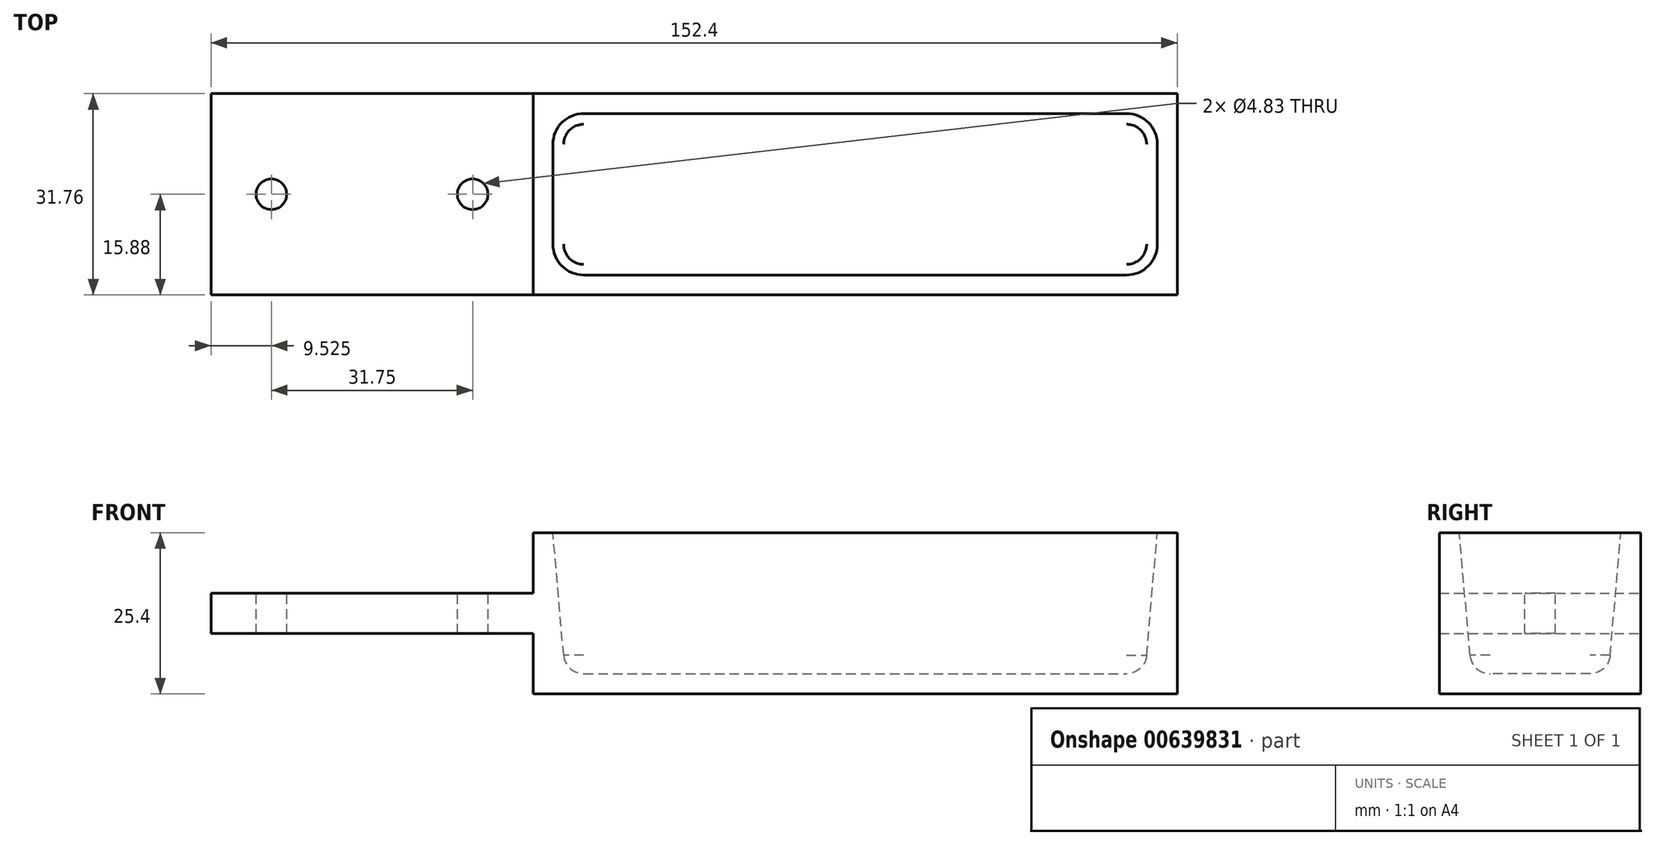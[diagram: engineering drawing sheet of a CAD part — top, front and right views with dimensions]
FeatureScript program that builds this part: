
annotation { "Feature Type Name" : "Feature", "Feature Type Description" : "" }
export const myFeature = defineFeature(function(context is Context, id is Id, definition is map)
    precondition{}
    {
        {
            var Q0;
            Q0=qCreatedBy(makeId("Top.planeOp"),FACE);
            var sketch = newSketch(context, id + "F0", { "sketchPlane" : qUnion([Q0])});
            skLineSegment(sketch, "E0.bottom", {"start": v(-50.8, 15.88) * mm, "end": v(50.8, 15.88) * mm});
            skLineSegment(sketch, "E0.top", {"start": v(-50.8, -15.87) * mm, "end": v(50.8, -15.87) * mm});
            skLineSegment(sketch, "E0.left", {"start": v(-50.8, 15.87) * mm, "end": v(-50.8, -15.87) * mm, "construction": true});
            skLineSegment(sketch, "E0.right", {"start": v(50.8, 15.87) * mm, "end": v(50.8, -15.87) * mm});
            skPoint(sketch, "E1", {"position": v(0, 15.88) * mm});
            skPoint(sketch, "E2", {"position": v(50.8, 0) * mm});
            skLineSegment(sketch, "E3", {"start": v(-50.8, 15.88) * mm, "end": v(-101.6, 15.88) * mm});
            skLineSegment(sketch, "E4", {"start": v(-101.6, 15.87) * mm, "end": v(-101.6, -15.87) * mm});
            skLineSegment(sketch, "E5", {"start": v(-101.6, -15.87) * mm, "end": v(-50.8, -15.87) * mm});
            skSolve(sketch);
        }
        {
            var Q0;
            Q0=makeQuery(id+"F0.imprint","IMPRINT",FACE,{"disambiguationData":[TD([[makeQuery(id+"F0.imprint","IMPRINT",EDGE,{"derivedFrom":sQuery(id+"F0.wireOp",EDGE,"E0.bottom")}),-1.0]])]});
            var Q1;
            Q1=sQuery(id+"F0.wireOp",EDGE,"E0.left");
            extrude(context, id + "F1", {"entities" : qUnion([Q0]), "surfaceEntities" : qUnion([Q1]), "depth" : 25.4 * mm, "offsetDistance" : 25.4 * mm});
        }
        {
            var Q0;
            Q0=qCreatedBy(makeId("Front.planeOp"),FACE);
            var sketch = newSketch(context, id + "F2", { "sketchPlane" : qUnion([Q0])});
            skLineSegment(sketch, "E6.bottom", {"start": v(-101.6, 25.4) * mm, "end": v(-50.8, 25.4) * mm});
            skLineSegment(sketch, "E6.top", {"start": v(-101.6, 15.88) * mm, "end": v(-50.8, 15.88) * mm});
            skLineSegment(sketch, "E6.left", {"start": v(-101.6, 25.4) * mm, "end": v(-101.6, 15.88) * mm});
            skLineSegment(sketch, "E6.right", {"start": v(-50.8, 25.4) * mm, "end": v(-50.8, 15.88) * mm});
            skLineSegment(sketch, "E7.bottom", {"start": v(-101.6, 0) * mm, "end": v(-50.8, 0) * mm});
            skLineSegment(sketch, "E7.top", {"start": v(-101.6, 9.53) * mm, "end": v(-50.8, 9.53) * mm});
            skLineSegment(sketch, "E7.left", {"start": v(-101.6, 0) * mm, "end": v(-101.6, 9.53) * mm});
            skLineSegment(sketch, "E7.right", {"start": v(-50.8, 0) * mm, "end": v(-50.8, 9.53) * mm});
            skSolve(sketch);
        }
        {
            var Q0;
            Q0 = qSketchRegion(id + "F2", true);
            extrude(context, id + "F3", {"entities" : qUnion([Q0]), "operationType" : NewBodyOperationType.REMOVE, "endBound" : BoundingType.THROUGH_ALL, "depth" : 25.4 * mm, "offsetDistance" : 25.4 * mm, "hasSecondDirection" : true, "secondDirectionOppositeDirection" : true, "secondDirectionDepth" : 50.8 * mm});
        }
        {
            var Q0;
            Q0=qCreatedBy(makeId("Front.planeOp"),FACE);
            var sketch = newSketch(context, id + "F4", { "sketchPlane" : qUnion([Q0])});
            skLineSegment(sketch, "E8", {"start": v(47.38, 22.18) * mm, "end": v(45.97, 6.07) * mm});
            skLineSegment(sketch, "E9", {"start": v(42.81, 25.4) * mm, "end": v(42.81, 3.18) * mm, "construction": true});
            skArc(sketch, "E10.filletArc", {"start": v(42.81, 3.18) * mm, "mid": v(44.96, 4) * mm, "end": v(45.97, 6.07) * mm});
            skPoint(sketch, "E11", {"position": v(47.38, 22.18) * mm});
            skLineSegment(sketch, "E12", {"start": v(47.38, 22.18) * mm, "end": v(47.89, 27.94) * mm});
            skLineSegment(sketch, "E13", {"start": v(45.97, 6.07) * mm, "end": v(45.72, 3.17) * mm, "construction": true});
            skLineSegment(sketch, "E14", {"start": v(45.72, 3.18) * mm, "end": v(42.81, 3.18) * mm, "construction": true});
            skPoint(sketch, "E15", {"position": v(47.66, 25.4) * mm});
            skLineSegment(sketch, "E16.0.1", {"start": v(-50.8, 25.4) * mm, "end": v(50.8, 25.4) * mm});
            skLineSegment(sketch, "E16.0.3", {"start": v(50.8, 25.4) * mm, "end": v(-50.8, 25.4) * mm});
            skSolve(sketch);
        }
        {
            var Q0;
            Q0=qCreatedBy(makeId("Right.planeOp"),FACE);
            var sketch = newSketch(context, id + "F5", { "sketchPlane" : qUnion([Q0])});
            skLineSegment(sketch, "E17.0", {"start": v(15.88, 25.4) * mm, "end": v(-15.87, 25.4) * mm});
            skLineSegment(sketch, "E18.0", {"start": v(15.88, 0) * mm, "end": v(-15.87, 0) * mm});
            skLineSegment(sketch, "E19.0", {"start": v(15.88, 25.4) * mm, "end": v(15.88, 0) * mm});
            skLineSegment(sketch, "E20", {"start": v(12.74, 25.4) * mm, "end": v(11.05, 6.07) * mm});
            skLineSegment(sketch, "E21", {"start": v(7.89, 3.18) * mm, "end": v(0, 3.18) * mm});
            skPoint(sketch, "E22.visualSharp", {"position": v(10.8, 3.18) * mm});
            skArc(sketch, "E22.filletArc", {"start": v(7.89, 3.18) * mm, "mid": v(10.03, 4) * mm, "end": v(11.05, 6.07) * mm});
            skLineSegment(sketch, "E23", {"start": v(11.05, 6.07) * mm, "end": v(10.8, 3.18) * mm, "construction": true});
            skLineSegment(sketch, "E24", {"start": v(7.89, 3.18) * mm, "end": v(10.8, 3.18) * mm, "construction": true});
            skLineSegment(sketch, "E25", {"start": v(11.43, 25.4) * mm, "end": v(11.43, 20.32) * mm});
            skLineSegment(sketch, "E26", {"start": v(11.43, 20.32) * mm, "end": v(10.92, 20.32) * mm});
            skLineSegment(sketch, "E27", {"start": v(10.92, 20.32) * mm, "end": v(10.92, 15.24) * mm});
            skLineSegment(sketch, "E28", {"start": v(10.92, 15.24) * mm, "end": v(10.41, 15.24) * mm});
            skLineSegment(sketch, "E29", {"start": v(10.41, 15.24) * mm, "end": v(10.41, 10.16) * mm});
            skLineSegment(sketch, "E30", {"start": v(10.41, 10.16) * mm, "end": v(9.9, 10.16) * mm});
            skLineSegment(sketch, "E31", {"start": v(9.9, 10.16) * mm, "end": v(9.9, 5.08) * mm});
            skLineSegment(sketch, "E32", {"start": v(9.9, 5.08) * mm, "end": v(7.37, 5.08) * mm});
            skLineSegment(sketch, "E33", {"start": v(7.37, 5.08) * mm, "end": v(7.37, 3.18) * mm});
            skLineSegment(sketch, "E34", {"start": v(11.46, 25.4) * mm, "end": v(9.52, 3.18) * mm});
            skLineSegment(sketch, "E35", {"start": v(10.92, 17.11) * mm, "end": v(1.44, 17.11) * mm});
            skPoint(sketch, "E36", {"position": v(6.18, 17.11) * mm});
            skSolve(sketch);
        }
        {
            var Q0;
            Q0=qCreatedBy(makeId("Front.planeOp"),FACE);
            var sketch = newSketch(context, id + "F6", { "sketchPlane" : qUnion([Q0])});
            skLineSegment(sketch, "E37.0", {"start": v(47.38, 22.18) * mm, "end": v(45.97, 6.07) * mm});
            skLineSegment(sketch, "E38.0", {"start": v(47.38, 22.18) * mm, "end": v(47.89, 27.94) * mm});
            skLineSegment(sketch, "E39.0.1", {"start": v(-50.8, 25.4) * mm, "end": v(50.8, 25.4) * mm});
            skLineSegment(sketch, "E39.0.3", {"start": v(50.8, 25.4) * mm, "end": v(-50.8, 25.4) * mm});
            skLineSegment(sketch, "E40", {"start": v(46.23, 25.4) * mm, "end": v(46.23, 20.32) * mm});
            skLineSegment(sketch, "E41", {"start": v(46.23, 20.32) * mm, "end": v(45.72, 20.32) * mm});
            skLineSegment(sketch, "E42", {"start": v(45.72, 20.32) * mm, "end": v(45.72, 15.24) * mm});
            skLineSegment(sketch, "E43", {"start": v(45.72, 15.24) * mm, "end": v(45.21, 15.24) * mm});
            skLineSegment(sketch, "E44", {"start": v(45.21, 15.24) * mm, "end": v(45.21, 10.16) * mm});
            skLineSegment(sketch, "E45", {"start": v(45.21, 10.16) * mm, "end": v(44.7, 10.16) * mm});
            skLineSegment(sketch, "E46", {"start": v(44.7, 10.16) * mm, "end": v(44.7, 5.08) * mm});
            skLineSegment(sketch, "E47", {"start": v(44.7, 5.08) * mm, "end": v(42.16, 5.08) * mm});
            skLineSegment(sketch, "E48", {"start": v(42.16, 5.08) * mm, "end": v(42.16, 3.18) * mm});
            skLineSegment(sketch, "E49", {"start": v(46.39, 25.4) * mm, "end": v(44.17, 0) * mm});
            skLineSegment(sketch, "E50.0", {"start": v(42.81, 25.4) * mm, "end": v(42.81, 3.18) * mm});
            skLineSegment(sketch, "E51", {"start": v(42.16, 3.18) * mm, "end": v(0, 3.17) * mm});
            skSolve(sketch);
        }
        {
            var Q0;
            Q0=makeQuery(id+"F1.opExtrude","CAP_FACE",FACE,{"disambiguationData":[OSD([sQuery(id+"F0.wireOp",EDGE,"E0.bottom"),sQuery(id+"F0.wireOp",EDGE,"E0.top"),sQuery(id+"F0.wireOp",EDGE,"E0.right"),sQuery(id+"F0.wireOp",EDGE,"E3"),sQuery(id+"F0.wireOp",EDGE,"E4"),sQuery(id+"F0.wireOp",EDGE,"E5")])],"isStart":true});
            cPlane(context, id + "F7", {"entities" : qUnion([Q0]), "cplaneType" : CPlaneType.OFFSET, "offset" : 3.17 * mm, "oppositeDirection" : true, "width" : 152.4 * mm, "height" : 152.4 * mm});
        }
        {
            var Q0;
            Q0=qCreatedBy(id+"F7.planeOp",FACE);
            var sketch = newSketch(context, id + "F8", { "sketchPlane" : qUnion([Q0])});
            skPoint(sketch, "E52.0", {"position": v(45.72, 0) * mm});
            skLineSegment(sketch, "E53.bottom", {"start": v(-42.81, -10.8) * mm, "end": v(42.81, -10.8) * mm});
            skLineSegment(sketch, "E53.top", {"start": v(-42.81, 10.8) * mm, "end": v(42.81, 10.8) * mm});
            skLineSegment(sketch, "E53.left", {"start": v(-45.72, -7.89) * mm, "end": v(-45.72, 7.89) * mm});
            skLineSegment(sketch, "E53.right", {"start": v(45.72, -7.89) * mm, "end": v(45.72, 7.89) * mm});
            skPoint(sketch, "E54", {"position": v(0, -10.8) * mm});
            skPoint(sketch, "E55.visualSharp", {"position": v(45.72, -10.8) * mm});
            skArc(sketch, "E55.filletArc", {"start": v(42.81, -10.8) * mm, "mid": v(44.87, -9.94) * mm, "end": v(45.72, -7.89) * mm});
            skPoint(sketch, "E56.visualSharp", {"position": v(45.72, 10.8) * mm});
            skArc(sketch, "E56.filletArc", {"start": v(45.72, 7.89) * mm, "mid": v(44.87, 9.94) * mm, "end": v(42.81, 10.8) * mm});
            skPoint(sketch, "E57.visualSharp", {"position": v(-45.72, -10.8) * mm});
            skArc(sketch, "E57.filletArc", {"start": v(-45.72, -7.89) * mm, "mid": v(-44.87, -9.94) * mm, "end": v(-42.81, -10.8) * mm});
            skPoint(sketch, "E58.visualSharp", {"position": v(-45.72, 10.8) * mm});
            skArc(sketch, "E58.filletArc", {"start": v(-42.81, 10.8) * mm, "mid": v(-44.87, 9.94) * mm, "end": v(-45.72, 7.89) * mm});
            skSolve(sketch);
        }
        {
            var Q0;
            Q0=makeQuery(id+"F8.imprint","IMPRINT",FACE,{"disambiguationData":[TD([[makeQuery(id+"F8.imprint","IMPRINT",EDGE,{"derivedFrom":sQuery(id+"F8.wireOp",EDGE,"E53.bottom")}),1.0]])]});
            extrude(context, id + "F9", {"entities" : qUnion([Q0]), "operationType" : NewBodyOperationType.REMOVE, "oppositeDirection" : true, "depth" : 25.4 * mm, "offsetDistance" : 25.4 * mm, "hasDraft" : true, "draftAngle" : 5 * degree});
        }
        {
            var Q0;
            Q0=makeQuery(id+"F9.boolean.opBoolean","COPY",EDGE,{"derivedFrom":makeQuery(id+"F9.opExtrude","CAP_EDGE",EDGE,{"disambiguationData":[OSD([sQuery(id+"F8.wireOp",EDGE,"E55.filletArc")])],"isStart":true})});
            fillet(context, id + "F10", {"entities" : qUnion([Q0]), "radius" : 3.17 * mm, "tangentPropagation" : true, "allowEdgeOverflow" : false});
        }
        {
            var Q0;
            Q0=makeQuery(id+"F1.opExtrude","CAP_FACE",FACE,{"disambiguationData":[OSD([sQuery(id+"F0.wireOp",EDGE,"E0.bottom"),sQuery(id+"F0.wireOp",EDGE,"E0.top"),sQuery(id+"F0.wireOp",EDGE,"E0.right"),sQuery(id+"F0.wireOp",EDGE,"E3"),sQuery(id+"F0.wireOp",EDGE,"E4"),sQuery(id+"F0.wireOp",EDGE,"E5")])],"isStart":false});
            var sketch = newSketch(context, id + "F11", { "sketchPlane" : qUnion([Q0])});
            skLineSegment(sketch, "E59.0", {"start": v(-50.8, 15.88) * mm, "end": v(50.8, 15.88) * mm});
            skLineSegment(sketch, "E60.0", {"start": v(42.81, 12.74) * mm, "end": v(-42.81, 12.74) * mm});
            skLineSegment(sketch, "E61.0", {"start": v(47.66, -7.89) * mm, "end": v(47.66, 7.89) * mm});
            skLineSegment(sketch, "E62.0", {"start": v(50.8, 15.88) * mm, "end": v(50.8, -15.87) * mm});
            skSolve(sketch);
        }
        {
            var Q0;
            Q0=makeQuery(id+"F3.boolean.opBoolean","COPY",FACE,{"derivedFrom":makeQuery(id+"F3.opExtrude","SWEPT_FACE",FACE,{"disambiguationData":[OSD([sQuery(id+"F2.wireOp",EDGE,"E6.top")])]})});
            var sketch = newSketch(context, id + "F12", { "sketchPlane" : qUnion([Q0])});
            skPoint(sketch, "E63", {"position": v(-92.08, 0) * mm});
            skPoint(sketch, "E64", {"position": v(-60.33, 0) * mm});
            skPoint(sketch, "E65", {"position": v(55.24, 0) * mm});
            skSolve(sketch);
        }
        {
            var Q0;
            Q0=sQuery(id+"F12.wireOp",VERTEX,"E63");
            var Q1;
            Q1=sQuery(id+"F12.wireOp",VERTEX,"E64");
            var Q2;
            Q2=makeQuery(id+"F1.opExtrude","SWEPT_BODY",BODY,{"disambiguationData":[OSD([sQuery(id+"F0.wireOp",EDGE,"E0.bottom"),sQuery(id+"F0.wireOp",EDGE,"E0.top"),sQuery(id+"F0.wireOp",EDGE,"E0.right"),sQuery(id+"F0.wireOp",EDGE,"E3"),sQuery(id+"F0.wireOp",EDGE,"E4"),sQuery(id+"F0.wireOp",EDGE,"E5")])]});
            hole(context, id + "F13", {"style" : HoleStyle.SIMPLE, "endStyle" : HoleEndStyle.THROUGH, "holeDiameter" : 4.83 * mm, "majorDiameter" : 6.35 * mm, "isTappedThrough" : true, "tappedDepth" : 12.7 * mm, "tapClearance" : 3, "startFromSketch" : true, "locations" : qUnion([Q0, Q1]), "scope" : qUnion([Q2])});
        }
        {
            var Q0;
            Q0=qCreatedBy(makeId("Front.planeOp"),FACE);
            var sketch = newSketch(context, id + "F14", { "sketchPlane" : qUnion([Q0])});
            skLineSegment(sketch, "E66.0", {"start": v(42.81, 25.4) * mm, "end": v(-42.81, 25.4) * mm});
            skLineSegment(sketch, "E67.bottom", {"start": v(42.04, 25.4) * mm, "end": v(35.69, 25.4) * mm});
            skLineSegment(sketch, "E67.top", {"start": v(42.04, 4.57) * mm, "end": v(35.69, 4.57) * mm});
            skLineSegment(sketch, "E67.left", {"start": v(42.04, 25.4) * mm, "end": v(42.04, 4.57) * mm});
            skLineSegment(sketch, "E67.right", {"start": v(35.69, 25.4) * mm, "end": v(35.69, 4.57) * mm});
            skPoint(sketch, "E68", {"position": v(38.86, 4.57) * mm});
            skLineSegment(sketch, "E69", {"start": v(38.86, 4.57) * mm, "end": v(38.86, 25.4) * mm});
            skSolve(sketch);
        }
        {
            var Q0;
            Q0=makeQuery(id+"F11.imprint","IMPRINT",FACE,{"disambiguationData":[TD([[makeQuery(id+"F11.imprint","IMPRINT",EDGE,{"derivedFrom":sQuery(id+"F11.wireOp",EDGE,"E59.0")}),-1.0]])]});
            var sketch = newSketch(context, id + "F15", { "sketchPlane" : qUnion([Q0])});
            skLineSegment(sketch, "E70.bottom", {"start": v(-43.18, 11.56) * mm, "end": v(43.18, 11.56) * mm});
            skLineSegment(sketch, "E70.top", {"start": v(-46.35, -11.56) * mm, "end": v(46.35, -11.56) * mm});
            skLineSegment(sketch, "E70.left", {"start": v(-46.35, 8.38) * mm, "end": v(-46.35, -11.56) * mm});
            skLineSegment(sketch, "E70.right", {"start": v(46.35, 8.38) * mm, "end": v(46.35, -11.56) * mm});
            skPoint(sketch, "E71", {"position": v(0, 11.56) * mm});
            skPoint(sketch, "E72", {"position": v(46.35, 0) * mm});
            skPoint(sketch, "E73.visualSharp", {"position": v(-46.35, 11.56) * mm});
            skArc(sketch, "E73.filletArc", {"start": v(-43.18, 11.56) * mm, "mid": v(-45.43, 10.63) * mm, "end": v(-46.35, 8.38) * mm});
            skPoint(sketch, "E74.visualSharp", {"position": v(46.35, 11.56) * mm});
            skArc(sketch, "E74.filletArc", {"start": v(46.35, 8.38) * mm, "mid": v(45.43, 10.63) * mm, "end": v(43.18, 11.56) * mm});
            skSolve(sketch);
        }
        {
            var Q0;
            Q0=makeQuery(id+"F11.imprint","IMPRINT",FACE,{"disambiguationData":[TD([[makeQuery(id+"F11.imprint","IMPRINT",EDGE,{"derivedFrom":sQuery(id+"F11.wireOp",EDGE,"E59.0")}),-1.0]])]});
            cPlane(context, id + "F16", {"entities" : qUnion([Q0]), "cplaneType" : CPlaneType.OFFSET, "offset" : 5.08 * mm, "oppositeDirection" : true, "width" : 152.4 * mm, "height" : 152.4 * mm});
        }
    });
